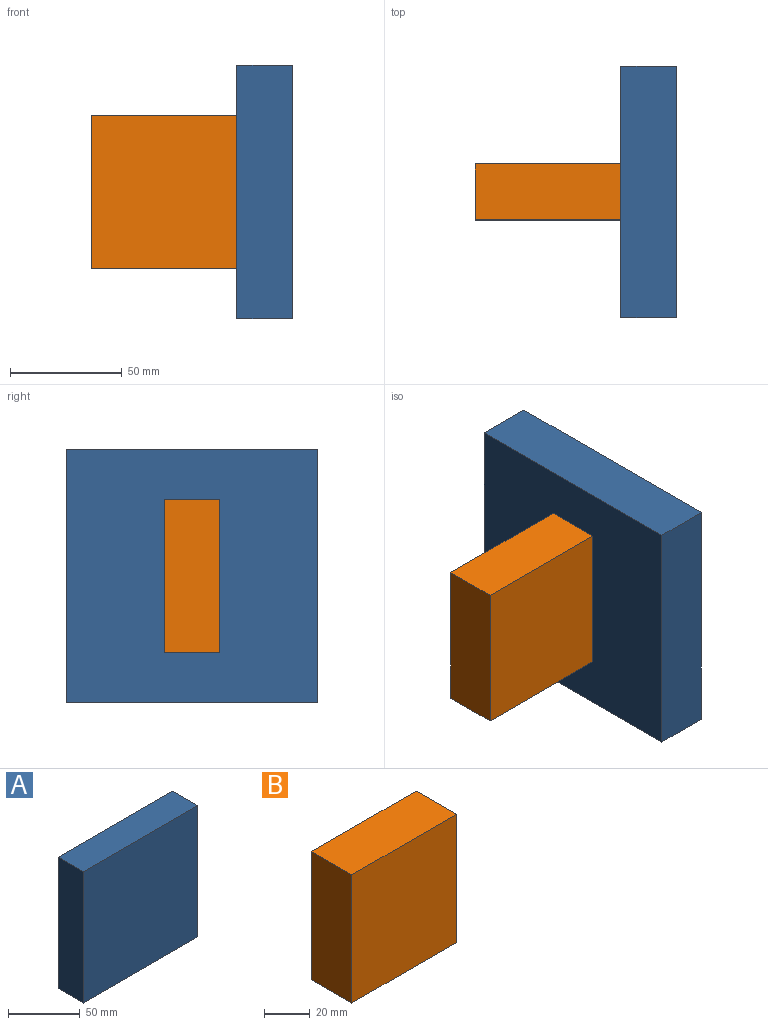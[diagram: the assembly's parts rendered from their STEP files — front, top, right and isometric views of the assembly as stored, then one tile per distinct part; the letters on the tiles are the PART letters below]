
ASSEMBLY  parts=2 mates=1
PART A: 6 faces, bbox 113.2x25x112.2 mm
  f0: plane 113.2x25mm, normal (0,0,-1), area 2830.1mm2, adj f1,f3,f4,f5
  f1: plane 112.25x25mm, normal (1,0,0), area 2806.2mm2, adj f0,f2,f4,f5
  f2: plane 113.2x25mm, normal (0,0,1), area 2830.1mm2, adj f1,f3,f4,f5
  f3: plane 112.25x25mm, normal (-1,0,0), area 2806.2mm2, adj f0,f2,f4,f5
  f4: plane 113.2x112.25mm, normal (0,-1,0), area 12707mm2, adj f0,f1,f2,f3
  f5: plane 113.2x112.25mm, normal (0,1,0), area 12707mm2, adj f0,f1,f2,f3
PART B: 6 faces, bbox 65x25x68.8 mm
  f0: plane 65.01x25mm, normal (0,0,-1), area 1625.2mm2, adj f1,f3,f4,f5
  f1: plane 68.81x25mm, normal (1,0,0), area 1720.1mm2, adj f0,f2,f4,f5
  f2: plane 65.01x25mm, normal (0,0,1), area 1625.2mm2, adj f1,f3,f4,f5
  f3: plane 68.81x25mm, normal (-1,0,0), area 1720.1mm2, adj f0,f2,f4,f5
  f4: plane 68.81x65.01mm, normal (0,-1,0), area 4473mm2, adj f0,f1,f2,f3
  f5: plane 68.81x65.01mm, normal (0,1,0), area 4473mm2, adj f0,f1,f2,f3
PLACE A rot(axis=(0.58,0.58,-0.58),120deg) t=(86.84,-10.4,36.08)mm
PLACE B t=(-3.17,2.1,1.68)mm fixed
MATE parallel B.f1 <-> A.f4  axis (1,0,0) through (61.84,-10.4,36.08)mm
